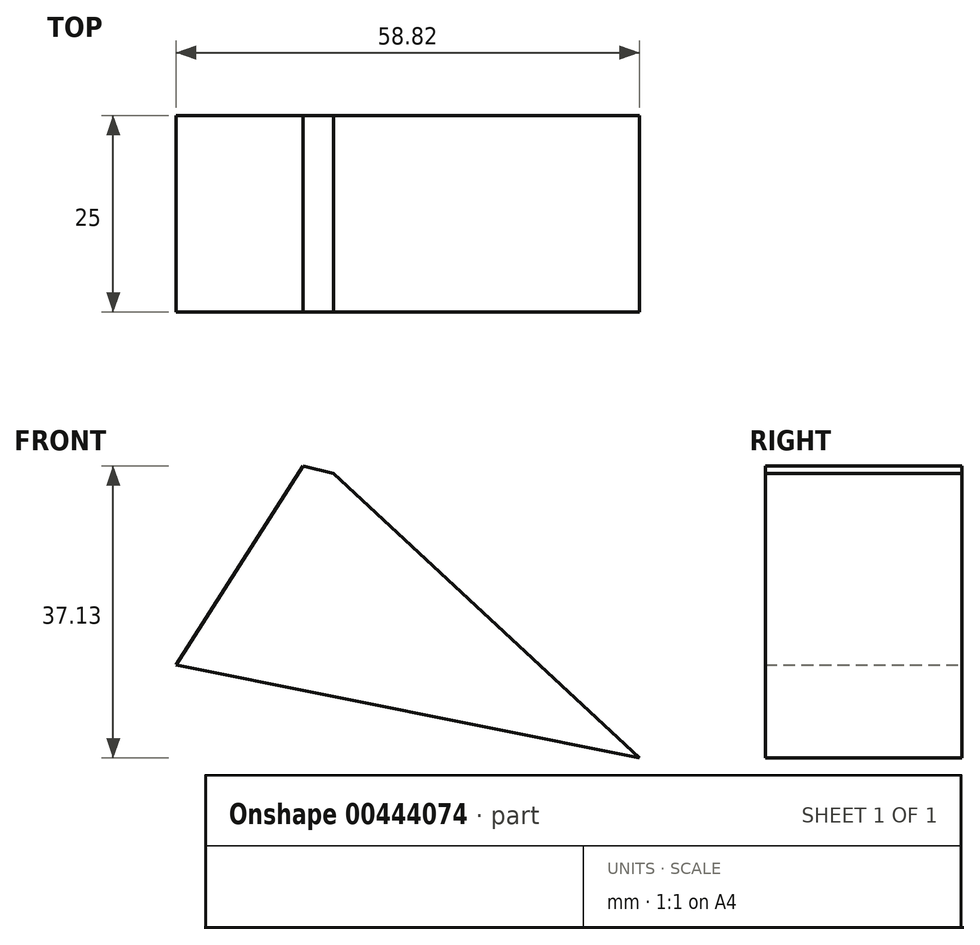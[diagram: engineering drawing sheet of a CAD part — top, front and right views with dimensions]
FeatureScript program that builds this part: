
annotation { "Feature Type Name" : "Feature", "Feature Type Description" : "" }
export const myFeature = defineFeature(function(context is Context, id is Id, definition is map)
    precondition{}
    {
        {
            var Q0;
            Q0=qCreatedBy(makeId("Front.planeOp"),FACE);
            var sketch = newSketch(context, id + "F0", { "sketchPlane" : qUnion([Q0])});
            skLineSegment(sketch, "E0", {"start": v(-61.04, 35.62) * mm, "end": v(-44.9, 60.91) * mm});
            skLineSegment(sketch, "E1", {"start": v(-44.9, 60.91) * mm, "end": v(-41.03, 59.95) * mm});
            skLineSegment(sketch, "E2", {"start": v(-41.03, 59.95) * mm, "end": v(-2.22, 23.78) * mm});
            skLineSegment(sketch, "E3", {"start": v(-2.22, 23.78) * mm, "end": v(-61.04, 35.62) * mm});
            skSolve(sketch);
        }
        {
            var Q0;
            Q0=makeQuery(id+"F0.imprint","IMPRINT",FACE,{"disambiguationData":[TD([[makeQuery(id+"F0.imprint","IMPRINT",EDGE,{"derivedFrom":sQuery(id+"F0.wireOp",EDGE,"E0")}),-1.0]])]});
            extrude(context, id + "F1", {"entities" : qUnion([Q0]), "depth" : 25 * mm});
        }
    });
